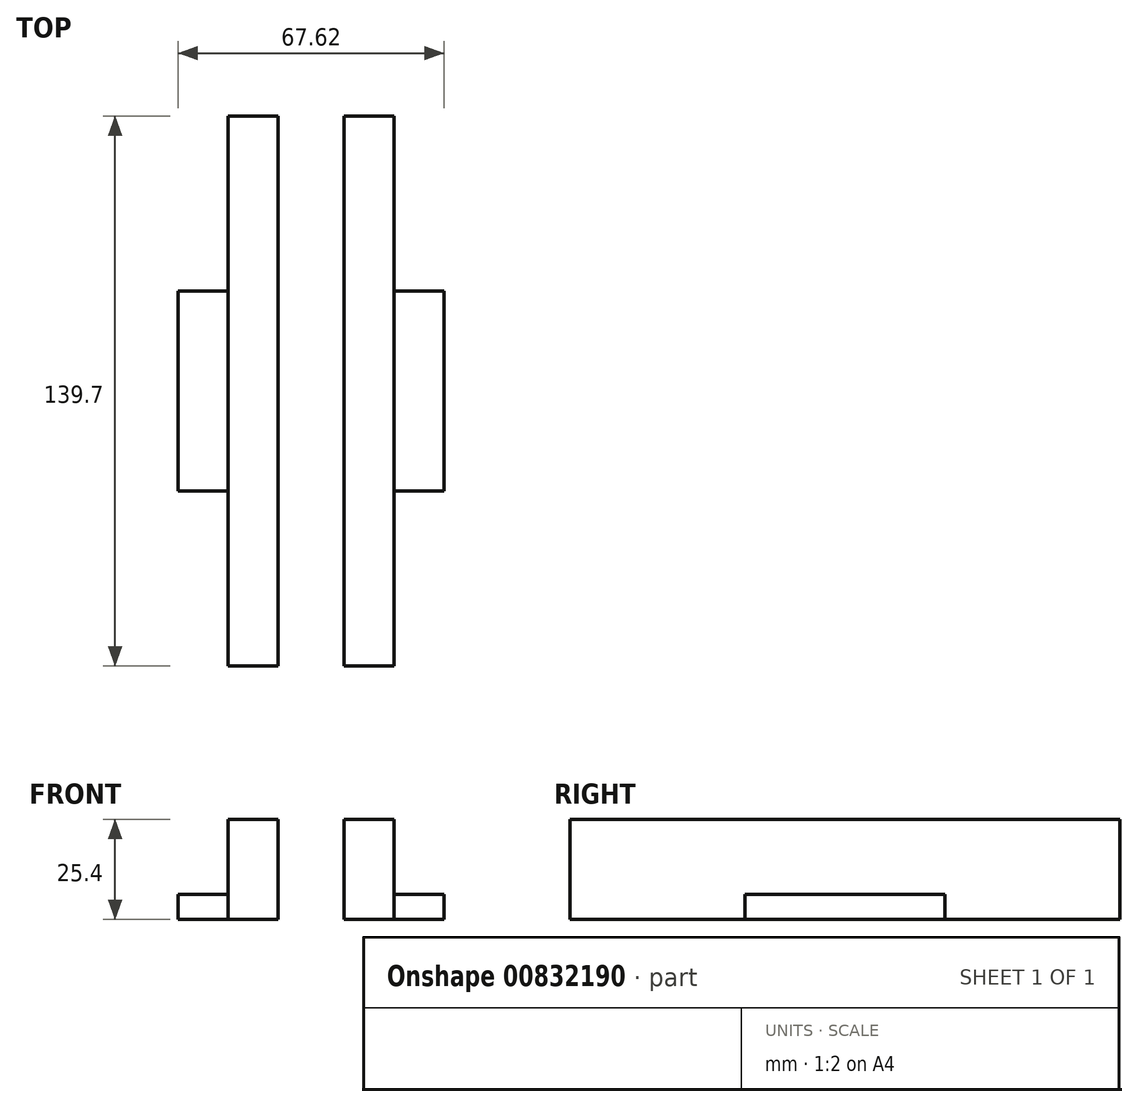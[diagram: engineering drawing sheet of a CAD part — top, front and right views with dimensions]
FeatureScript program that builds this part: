
annotation { "Feature Type Name" : "Feature", "Feature Type Description" : "" }
export const myFeature = defineFeature(function(context is Context, id is Id, definition is map)
    precondition{}
    {
        {
            var Q0;
            Q0=qCreatedBy(makeId("Top.planeOp"),FACE);
            var sketch = newSketch(context, id + "F0", { "sketchPlane" : qUnion([Q0])});
            skLineSegment(sketch, "E0.bottom", {"start": v(-8.4, -69.85) * mm, "end": v(-21.1, -69.85) * mm});
            skLineSegment(sketch, "E0.top", {"start": v(-8.4, 69.85) * mm, "end": v(-21.1, 69.85) * mm});
            skLineSegment(sketch, "E0.left", {"start": v(-8.4, -69.85) * mm, "end": v(-8.4, 69.85) * mm});
            skLineSegment(sketch, "E0.right", {"start": v(-21.1, -69.85) * mm, "end": v(-21.1, 69.85) * mm});
            skLineSegment(sketch, "E1.MirrorCS", {"start": v(8.4, -69.85) * mm, "end": v(8.4, 69.85) * mm});
            skLineSegment(sketch, "E2.MirrorCS", {"start": v(21.1, -69.85) * mm, "end": v(21.1, 69.85) * mm});
            skLineSegment(sketch, "E3.MirrorCS", {"start": v(8.4, -69.85) * mm, "end": v(21.1, -69.85) * mm});
            skLineSegment(sketch, "E4.MirrorCS", {"start": v(8.4, 69.85) * mm, "end": v(21.1, 69.85) * mm});
            skSolve(sketch);
        }
        {
            var Q0;
            Q0=makeQuery(id+"F0.imprint","IMPRINT",FACE,{"disambiguationData":[TD([[makeQuery(id+"F0.imprint","IMPRINT",EDGE,{"derivedFrom":sQuery(id+"F0.wireOp",EDGE,"E0.bottom")}),-1.0]])]});
            var Q1;
            Q1=makeQuery(id+"F0.imprint","IMPRINT",FACE,{"disambiguationData":[TD([[makeQuery(id+"F0.imprint","IMPRINT",EDGE,{"derivedFrom":sQuery(id+"F0.wireOp",EDGE,"E1.MirrorCS")}),-1.0]])]});
            extrude(context, id + "F1", {"entities" : qUnion([Q0, Q1]), "depth" : 25.4 * mm, "offsetDistance" : 25.4 * mm});
        }
        {
            var Q0;
            Q0=makeQuery(id+"F1.opExtrude","SWEPT_FACE",FACE,{"disambiguationData":[OSD([sQuery(id+"F0.wireOp",EDGE,"E2.MirrorCS")])]});
            var sketch = newSketch(context, id + "F2", { "sketchPlane" : qUnion([Q0])});
            skLineSegment(sketch, "E5.bottom", {"start": v(-25.4, 0) * mm, "end": v(25.4, 0) * mm});
            skLineSegment(sketch, "E5.top", {"start": v(-25.4, 6.35) * mm, "end": v(25.4, 6.35) * mm});
            skLineSegment(sketch, "E5.left", {"start": v(-25.4, 0) * mm, "end": v(-25.4, 6.35) * mm});
            skLineSegment(sketch, "E5.right", {"start": v(25.4, 0) * mm, "end": v(25.4, 6.35) * mm});
            skSolve(sketch);
        }
        {
            var Q0;
            Q0=makeQuery(id+"F1.opExtrude","SWEPT_FACE",FACE,{"disambiguationData":[OSD([sQuery(id+"F0.wireOp",EDGE,"E0.right")])]});
            var sketch = newSketch(context, id + "F3", { "sketchPlane" : qUnion([Q0])});
            skLineSegment(sketch, "E6.bottom", {"start": v(-25.4, 0) * mm, "end": v(25.4, 0) * mm});
            skLineSegment(sketch, "E6.top", {"start": v(-25.4, 6.35) * mm, "end": v(25.4, 6.35) * mm});
            skLineSegment(sketch, "E6.left", {"start": v(-25.4, 0) * mm, "end": v(-25.4, 6.35) * mm});
            skLineSegment(sketch, "E6.right", {"start": v(25.4, 0) * mm, "end": v(25.4, 6.35) * mm});
            skSolve(sketch);
        }
        {
            var Q0;
            Q0=makeQuery(id+"F2.imprint","IMPRINT",FACE,{"disambiguationData":[TD([[makeQuery(id+"F2.imprint","IMPRINT",EDGE,{"derivedFrom":sQuery(id+"F2.wireOp",EDGE,"E5.top")}),-1.0]])]});
            extrude(context, id + "F4", {"entities" : qUnion([Q0]), "operationType" : NewBodyOperationType.ADD, "depth" : 12.7 * mm, "offsetDistance" : 25.4 * mm});
        }
        {
            var Q0;
            Q0=makeQuery(id+"F3.imprint","IMPRINT",FACE,{"disambiguationData":[TD([[makeQuery(id+"F3.imprint","IMPRINT",EDGE,{"derivedFrom":sQuery(id+"F3.wireOp",EDGE,"E6.bottom")}),-1.0]])]});
            extrude(context, id + "F5", {"entities" : qUnion([Q0]), "operationType" : NewBodyOperationType.ADD, "depth" : 12.7 * mm, "offsetDistance" : 25.4 * mm});
        }
    });
